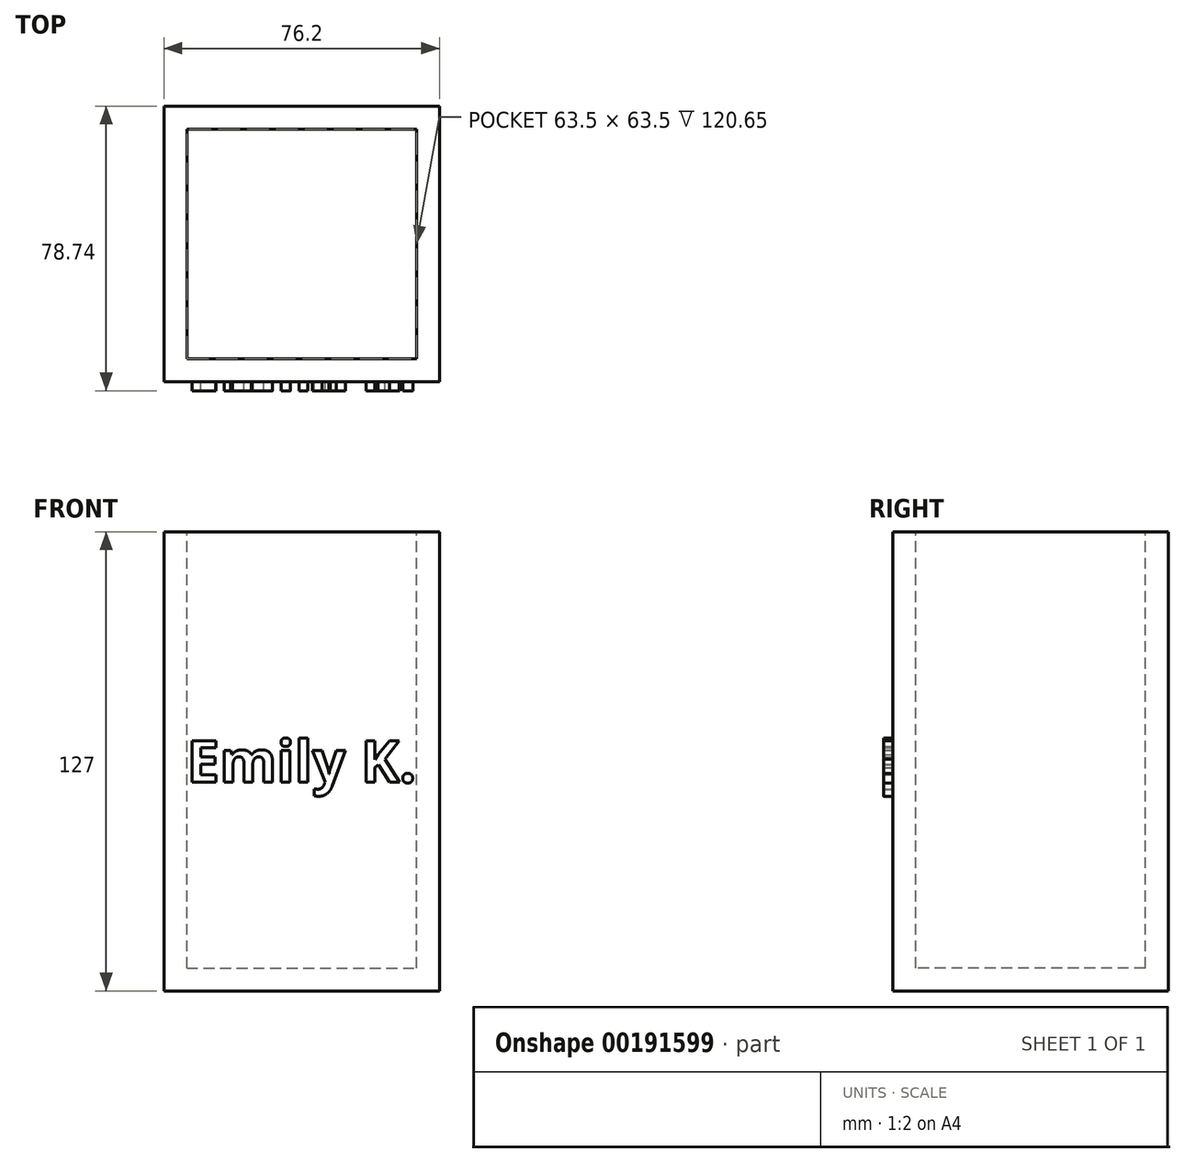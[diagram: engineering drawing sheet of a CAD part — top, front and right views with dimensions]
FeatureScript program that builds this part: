
annotation { "Feature Type Name" : "Feature", "Feature Type Description" : "" }
export const myFeature = defineFeature(function(context is Context, id is Id, definition is map)
    precondition{}
    {
        {
            var Q0;
            Q0=qCreatedBy(makeId("Front.planeOp"),FACE);
            var sketch = newSketch(context, id + "F0", { "sketchPlane" : qUnion([Q0])});
            skLineSegment(sketch, "E0.bottom", {"start": v(-43.74, 101.96) * mm, "end": v(32.46, 101.96) * mm});
            skLineSegment(sketch, "E0.top", {"start": v(-43.74, -25.04) * mm, "end": v(32.46, -25.04) * mm});
            skLineSegment(sketch, "E0.left", {"start": v(-43.74, 101.96) * mm, "end": v(-43.74, -25.04) * mm});
            skLineSegment(sketch, "E0.right", {"start": v(32.46, 101.96) * mm, "end": v(32.46, -25.04) * mm});
            skSolve(sketch);
        }
        {
            var Q0;
            Q0 = qSketchRegion(id + "F0", true);
            extrude(context, id + "F1", {"entities" : qUnion([Q0]), "depth" : 76.2 * mm});
        }
        {
            var Q0;
            Q0=makeQuery(id+"F1.opExtrude","SWEPT_FACE",FACE,{"disambiguationData":[OSD([sQuery(id+"F0.wireOp",EDGE,"E0.bottom")])]});
            var sketch = newSketch(context, id + "F2", { "sketchPlane" : qUnion([Q0])});
            skLineSegment(sketch, "E1.bottom", {"start": v(-37.39, -6.35) * mm, "end": v(26.11, -6.35) * mm});
            skLineSegment(sketch, "E1.top", {"start": v(-37.39, -69.85) * mm, "end": v(26.11, -69.85) * mm});
            skLineSegment(sketch, "E1.left", {"start": v(-37.39, -6.35) * mm, "end": v(-37.39, -69.85) * mm});
            skLineSegment(sketch, "E1.right", {"start": v(26.11, -6.35) * mm, "end": v(26.11, -69.85) * mm});
            skSolve(sketch);
        }
        {
            var Q0;
            Q0 = qSketchRegion(id + "F2", true);
            extrude(context, id + "F3", {"entities" : qUnion([Q0]), "operationType" : NewBodyOperationType.REMOVE, "oppositeDirection" : true, "depth" : 120.65 * mm});
        }
        {
            var Q0;
            Q0=makeQuery(id+"F1.opExtrude","CAP_FACE",FACE,{"disambiguationData":[OSD([sQuery(id+"F0.wireOp",EDGE,"E0.bottom"),sQuery(id+"F0.wireOp",EDGE,"E0.top"),sQuery(id+"F0.wireOp",EDGE,"E0.left"),sQuery(id+"F0.wireOp",EDGE,"E0.right")])],"isStart":false});
            var sketch = newSketch(context, id + "F4", { "sketchPlane" : qUnion([Q0])});
            skText(sketch, "E2", { "text": "Emily K.", "fontName": "OpenSans-Bold.ttf"});
            const initialGuessF4  = {"E2": [-0.03739, 0.03266, 1, 0, 0.01161]};
            skSetInitialGuess(sketch, initialGuessF4);
            skSolve(sketch);
        }
        {
            var Q0;
            Q0 = qSketchRegion(id + "F4", true);
            extrude(context, id + "F5", {"entities" : qUnion([Q0]), "operationType" : NewBodyOperationType.ADD, "depth" : 2.54 * mm});
        }
    });
